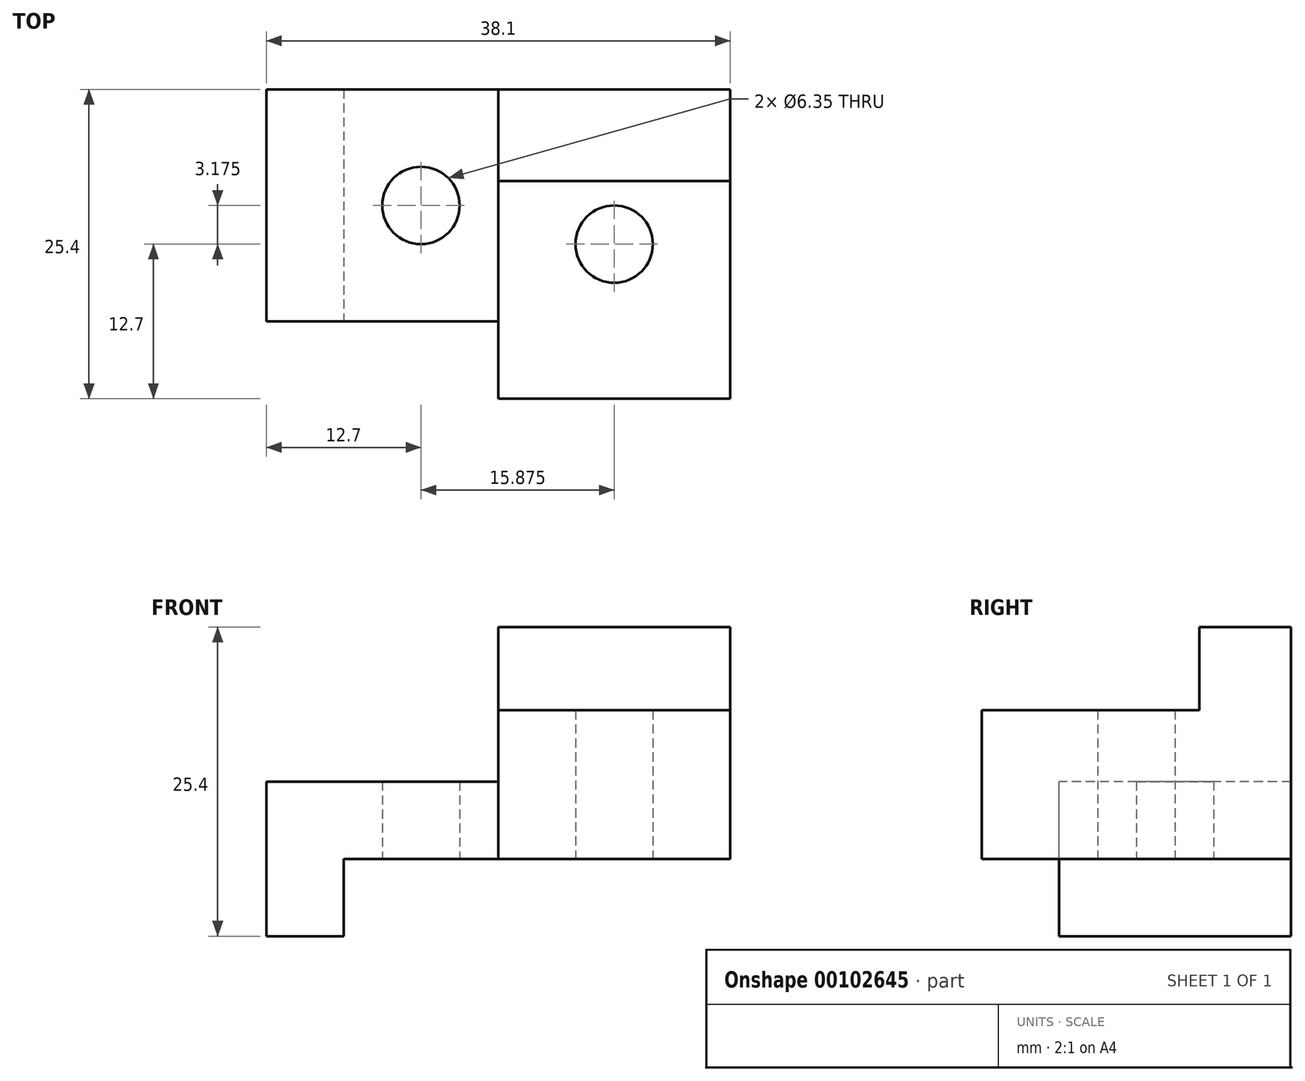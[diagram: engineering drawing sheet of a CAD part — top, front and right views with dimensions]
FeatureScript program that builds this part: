
annotation { "Feature Type Name" : "Feature", "Feature Type Description" : "" }
export const myFeature = defineFeature(function(context is Context, id is Id, definition is map)
    precondition{}
    {
        {
            var Q0;
            Q0=qCreatedBy(makeId("Top.planeOp"),FACE);
            var sketch = newSketch(context, id + "F0", { "sketchPlane" : qUnion([Q0])});
            skPoint(sketch, "E0.0", {"position": v(0, 0) * mm});
            skLineSegment(sketch, "E1", {"start": v(0, 0) * mm, "end": v(19.05, 0) * mm});
            skLineSegment(sketch, "E2", {"start": v(19.05, 0) * mm, "end": v(19.05, 25.4) * mm});
            skLineSegment(sketch, "E3", {"start": v(19.05, 25.4) * mm, "end": v(0, 25.4) * mm});
            skLineSegment(sketch, "E4", {"start": v(0, 25.4) * mm, "end": v(0, 0) * mm});
            skLineSegment(sketch, "E5", {"start": v(-19.05, 0) * mm, "end": v(-19.05, 25.4) * mm});
            skLineSegment(sketch, "E6", {"start": v(-19.05, 25.4) * mm, "end": v(0, 25.4) * mm});
            skLineSegment(sketch, "E7", {"start": v(-19.05, 0) * mm, "end": v(0, 0) * mm});
            skSolve(sketch);
        }
        {
            var Q0;
            Q0 = qSketchRegion(id + "F0", true);
            extrude(context, id + "F1", {"entities" : qUnion([Q0]), "endBound" : BoundingType.SYMMETRIC, "depth" : 25.4 * mm});
        }
        {
            var Q0;
            Q0=makeQuery(id+"F1.opExtrude","SWEPT_FACE",FACE,{"disambiguationData":[OSD([sQuery(id+"F0.wireOp",EDGE,"E1"),sQuery(id+"F0.wireOp",EDGE,"E7")])]});
            var sketch = newSketch(context, id + "F2", { "sketchPlane" : qUnion([Q0])});
            skLineSegment(sketch, "E8", {"start": v(-12.7, -12.7) * mm, "end": v(-12.7, -6.35) * mm});
            skLineSegment(sketch, "E9", {"start": v(-12.7, -6.35) * mm, "end": v(19.05, -6.35) * mm});
            skLineSegment(sketch, "E10", {"start": v(19.05, -6.35) * mm, "end": v(19.05, -12.7) * mm});
            skLineSegment(sketch, "E11", {"start": v(19.05, -12.7) * mm, "end": v(-12.7, -12.7) * mm});
            skSolve(sketch);
        }
        {
            var Q0;
            Q0=makeQuery(id+"F2.imprint","IMPRINT",FACE,{"disambiguationData":[TD([[makeQuery(id+"F2.imprint","IMPRINT",EDGE,{"derivedFrom":sQuery(id+"F2.wireOp",EDGE,"E8")}),-1.0]])]});
            extrude(context, id + "F3", {"entities" : qUnion([Q0]), "operationType" : NewBodyOperationType.REMOVE, "endBound" : BoundingType.THROUGH_ALL, "oppositeDirection" : true, "depth" : 25.4 * mm});
        }
        {
            var Q0;
            Q0=makeQuery(id+"F1.opExtrude","SWEPT_FACE",FACE,{"disambiguationData":[OSD([sQuery(id+"F0.wireOp",EDGE,"E1"),sQuery(id+"F0.wireOp",EDGE,"E7")])]});
            var sketch = newSketch(context, id + "F4", { "sketchPlane" : qUnion([Q0])});
            skLineSegment(sketch, "E12", {"start": v(-19.05, 0) * mm, "end": v(0, 0) * mm});
            skLineSegment(sketch, "E13", {"start": v(0, 0) * mm, "end": v(0, 12.7) * mm});
            skLineSegment(sketch, "E14", {"start": v(0, 12.7) * mm, "end": v(-19.05, 12.7) * mm});
            skLineSegment(sketch, "E15", {"start": v(-19.05, 12.7) * mm, "end": v(-19.05, 0) * mm});
            skSolve(sketch);
        }
        {
            var Q0;
            Q0=makeQuery(id+"F4.imprint","IMPRINT",FACE,{"disambiguationData":[TD([[makeQuery(id+"F4.imprint","IMPRINT",EDGE,{"derivedFrom":sQuery(id+"F4.wireOp",EDGE,"E12")}),1.0]])]});
            extrude(context, id + "F5", {"entities" : qUnion([Q0]), "operationType" : NewBodyOperationType.REMOVE, "endBound" : BoundingType.THROUGH_ALL, "oppositeDirection" : true, "depth" : 25.4 * mm});
        }
        {
            var Q0;
            Q0=makeQuery(id+"F1.opExtrude","SWEPT_FACE",FACE,{"disambiguationData":[OSD([sQuery(id+"F0.wireOp",EDGE,"E2")])]});
            var sketch = newSketch(context, id + "F6", { "sketchPlane" : qUnion([Q0])});
            skLineSegment(sketch, "E16", {"start": v(17.87, 12.7) * mm, "end": v(17.87, 5.85) * mm});
            skLineSegment(sketch, "E17", {"start": v(17.87, 5.85) * mm, "end": v(0, 5.85) * mm});
            skSolve(sketch);
        }
        {
            var Q0;
            {var subQ0=sQuery(id+"F6.wireOp",EDGE,"E16");Q0=makeQuery(id+"F6.imprint","IMPRINT",FACE,{"disambiguationData":[TD([[makeQuery(id+"F6.imprint","IMPRINT",EDGE,{"derivedFrom":subQ0}),-1.0]])]});}
            extrude(context, id + "F7", {"entities" : qUnion([Q0]), "operationType" : NewBodyOperationType.REMOVE, "endBound" : BoundingType.THROUGH_ALL, "oppositeDirection" : true, "depth" : 25.4 * mm});
        }
        {
            var Q0;
            Q0=makeQuery(id+"F5.boolean.opBoolean","COPY",FACE,{"derivedFrom":makeQuery(id+"F5.opExtrude","SWEPT_FACE",FACE,{"disambiguationData":[OSD([sQuery(id+"F4.wireOp",EDGE,"E12")])]})});
            var sketch = newSketch(context, id + "F8", { "sketchPlane" : qUnion([Q0])});
            skLineSegment(sketch, "E18", {"start": v(-19.05, 0) * mm, "end": v(0, 0) * mm});
            skLineSegment(sketch, "E19", {"start": v(0, 0) * mm, "end": v(0, 6.35) * mm});
            skLineSegment(sketch, "E20", {"start": v(0, 6.35) * mm, "end": v(-19.05, 6.35) * mm});
            skLineSegment(sketch, "E21", {"start": v(-19.05, 6.35) * mm, "end": v(-19.05, 0) * mm});
            skSolve(sketch);
        }
        {
            var Q0;
            Q0=makeQuery(id+"F8.imprint","IMPRINT",FACE,{"disambiguationData":[TD([[makeQuery(id+"F8.imprint","IMPRINT",EDGE,{"derivedFrom":sQuery(id+"F8.wireOp",EDGE,"E18")}),1.0]])]});
            extrude(context, id + "F9", {"entities" : qUnion([Q0]), "operationType" : NewBodyOperationType.REMOVE, "endBound" : BoundingType.THROUGH_ALL, "oppositeDirection" : true, "depth" : 25.4 * mm});
        }
        {
            var Q0;
            Q0=makeQuery(id+"F3.boolean.opBoolean","COPY",FACE,{"derivedFrom":makeQuery(id+"F3.opExtrude","SWEPT_FACE",FACE,{"disambiguationData":[OSD([sQuery(id+"F2.wireOp",EDGE,"E9")])]})});
            var sketch = newSketch(context, id + "F10", { "sketchPlane" : qUnion([Q0])});
            skCircle(sketch, "E22", {"center": v(-6.35, -15.88) * mm, "radius": 3.18 * mm});
            skPoint(sketch, "E22.centerSnap0", {"position": v(-12.7, -15.88) * mm});
            skPoint(sketch, "E22.centerSnap1", {"position": v(-6.35, -6.35) * mm});
            skCircle(sketch, "E23", {"center": v(9.52, -12.7) * mm, "radius": 3.18 * mm});
            skPoint(sketch, "E23.centerSnap0", {"position": v(9.52, 0) * mm});
            skPoint(sketch, "E23.centerSnap1", {"position": v(19.05, -12.7) * mm});
            skSolve(sketch);
        }
        {
            var Q0;
            Q0=makeQuery(id+"F10.imprint","IMPRINT",FACE,{"disambiguationData":[TD([[makeQuery(id+"F10.imprint","IMPRINT",EDGE,{"derivedFrom":sQuery(id+"F10.wireOp",EDGE,"E22")}),1.0]])]});
            var Q1;
            Q1=makeQuery(id+"F10.imprint","IMPRINT",FACE,{"disambiguationData":[TD([[makeQuery(id+"F10.imprint","IMPRINT",EDGE,{"derivedFrom":sQuery(id+"F10.wireOp",EDGE,"E23")}),1.0]])]});
            extrude(context, id + "F11", {"entities" : qUnion([Q0, Q1]), "operationType" : NewBodyOperationType.REMOVE, "endBound" : BoundingType.THROUGH_ALL, "oppositeDirection" : true, "depth" : 25.4 * mm, "hasSecondDirection" : true, "secondDirectionBound" : SecondDirectionBoundingType.THROUGH_ALL, "secondDirectionOppositeDirection" : false, "secondDirectionDepth" : 25.4 * mm});
        }
    });
